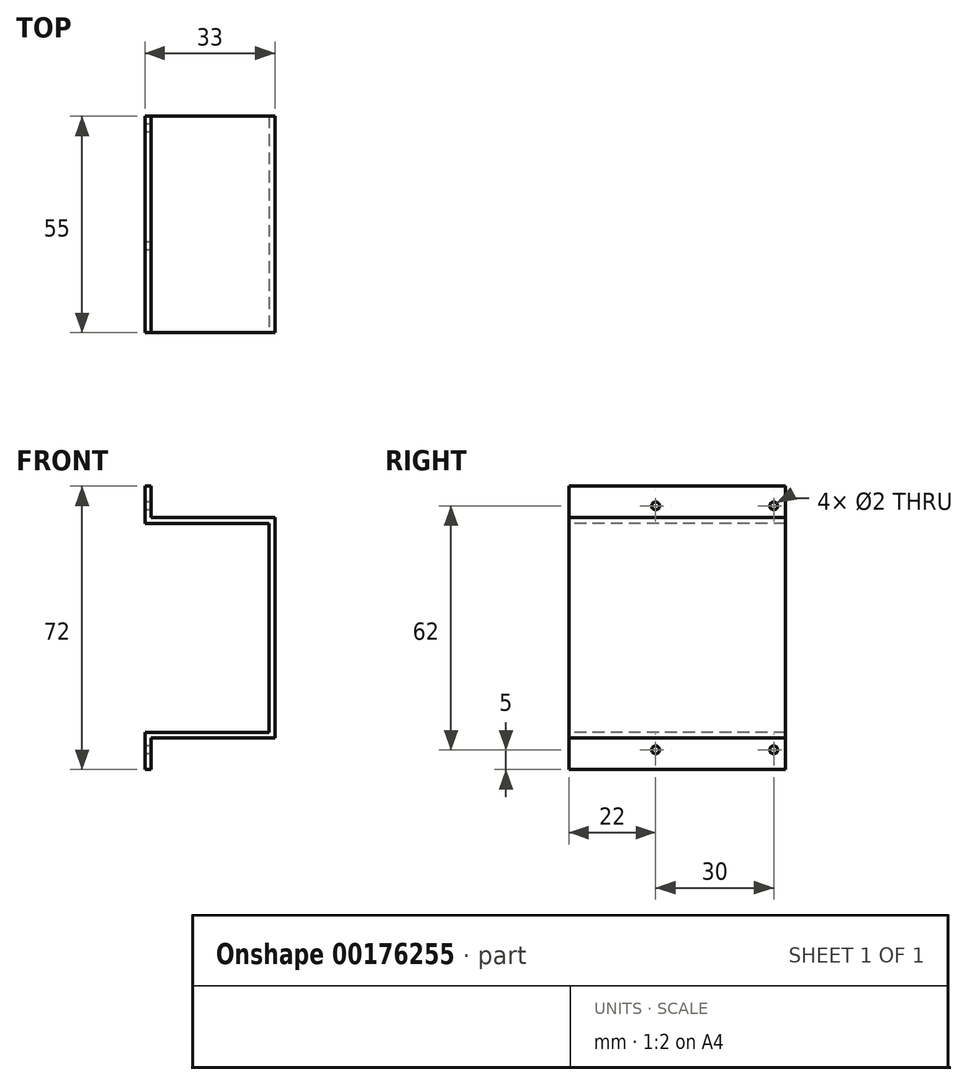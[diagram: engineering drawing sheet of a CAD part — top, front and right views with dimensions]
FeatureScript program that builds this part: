
annotation { "Feature Type Name" : "Feature", "Feature Type Description" : "" }
export const myFeature = defineFeature(function(context is Context, id is Id, definition is map)
    precondition{}
    {
        {
            var Q0;
            Q0=qCreatedBy(makeId("Top.planeOp"),FACE);
            var sketch = newSketch(context, id + "F0", { "sketchPlane" : qUnion([Q0])});
            skLineSegment(sketch, "E0.bottom", {"start": v(-15, 27.5) * mm, "end": v(15, 27.5) * mm});
            skLineSegment(sketch, "E0.top", {"start": v(-15, -27.5) * mm, "end": v(15, -27.5) * mm});
            skLineSegment(sketch, "E0.left", {"start": v(-15, 27.5) * mm, "end": v(-15, -27.5) * mm});
            skLineSegment(sketch, "E0.right", {"start": v(15, 27.5) * mm, "end": v(15, -27.5) * mm});
            skPoint(sketch, "E0.middle", {"position": v(0, 0) * mm});
            skSolve(sketch);
        }
        {
            var Q0;
            Q0 = qSketchRegion(id + "F0", true);
            extrude(context, id + "F1", {"entities" : qUnion([Q0]), "depth" : 1.5 * mm});
        }
        {
            var Q0;
            Q0=qCreatedBy(makeId("Top.planeOp"),FACE);
            var sketch = newSketch(context, id + "F2", { "sketchPlane" : qUnion([Q0])});
            skLineSegment(sketch, "E1.0", {"start": v(-15, 27.5) * mm, "end": v(-15, -27.5) * mm});
            skLineSegment(sketch, "E2", {"start": v(-15, 27.5) * mm, "end": v(-16.5, 27.5) * mm});
            skLineSegment(sketch, "E3", {"start": v(-16.5, 27.5) * mm, "end": v(-16.5, -27.5) * mm});
            skLineSegment(sketch, "E4", {"start": v(-16.5, -27.5) * mm, "end": v(-15, -27.5) * mm});
            skLineSegment(sketch, "E5.MirrorCS", {"start": v(15, 27.5) * mm, "end": v(16.5, 27.5) * mm});
            skLineSegment(sketch, "E6.MirrorCS", {"start": v(16.5, -27.5) * mm, "end": v(15, -27.5) * mm});
            skLineSegment(sketch, "E7.MirrorCS", {"start": v(15, 27.5) * mm, "end": v(15, -27.5) * mm});
            skLineSegment(sketch, "E8.MirrorCS", {"start": v(16.5, 27.5) * mm, "end": v(16.5, -27.5) * mm});
            skSolve(sketch);
        }
        {
            var Q0;
            Q0=makeQuery(id+"F2.imprint","IMPRINT",FACE,{"disambiguationData":[TD([[makeQuery(id+"F2.imprint","IMPRINT",EDGE,{"derivedFrom":sQuery(id+"F2.wireOp",EDGE,"E1.0")}),-1.0]])]});
            extrude(context, id + "F3", {"entities" : qUnion([Q0]), "operationType" : NewBodyOperationType.ADD, "depth" : 1.5 * mm, "hasSecondDirection" : true, "secondDirectionOppositeDirection" : true, "secondDirectionDepth" : 8 * mm});
        }
        {
            var Q0;
            Q0=makeQuery(id+"F2.imprint","IMPRINT",FACE,{"disambiguationData":[TD([[makeQuery(id+"F2.imprint","IMPRINT",EDGE,{"derivedFrom":sQuery(id+"F2.wireOp",EDGE,"E5.MirrorCS")}),-1.0]])]});
            extrude(context, id + "F4", {"entities" : qUnion([Q0]), "operationType" : NewBodyOperationType.ADD, "depth" : (26.5 + 1.5) * mm});
        }
        {
            var Q0;
            Q0=makeQuery(id+"F3.opExtrude","SWEPT_FACE",FACE,{"disambiguationData":[OSD([sQuery(id+"F2.wireOp",EDGE,"E3")])]});
            var sketch = newSketch(context, id + "F5", { "sketchPlane" : qUnion([Q0])});
            skCircle(sketch, "E9", {"center": v(-24.5, -3) * mm, "radius": 1 * mm});
            skCircle(sketch, "E10", {"center": v(5.5, -3) * mm, "radius": 1 * mm});
            skSolve(sketch);
        }
        {
            var Q0;
            Q0 = qSketchRegion(id + "F5", true);
            extrude(context, id + "F6", {"entities" : qUnion([Q0]), "operationType" : NewBodyOperationType.REMOVE, "endBound" : BoundingType.UP_TO_NEXT, "oppositeDirection" : true, "depth" : 25 * mm});
        }
        {
            var Q0;
            Q0=makeQuery(id+"F1.opExtrude","SWEPT_BODY",BODY,{"disambiguationData":[OSD([sQuery(id+"F0.wireOp",EDGE,"E0.bottom"),sQuery(id+"F0.wireOp",EDGE,"E0.top"),sQuery(id+"F0.wireOp",EDGE,"E0.left"),sQuery(id+"F0.wireOp",EDGE,"E0.right")])]});
            var Q1;
            Q1=makeQuery(id+"F4.opExtrude","CAP_FACE",FACE,{"disambiguationData":[OSD([sQuery(id+"F2.wireOp",EDGE,"E5.MirrorCS"),sQuery(id+"F2.wireOp",EDGE,"E6.MirrorCS"),sQuery(id+"F2.wireOp",EDGE,"E7.MirrorCS"),sQuery(id+"F2.wireOp",EDGE,"E8.MirrorCS")])],"isStart":false});
            mirror(context, id + "F7", {"operationType" : NewBodyOperationType.ADD, "entities" : qUnion([Q0]), "mirrorPlane" : qUnion([Q1])});
        }
    });
